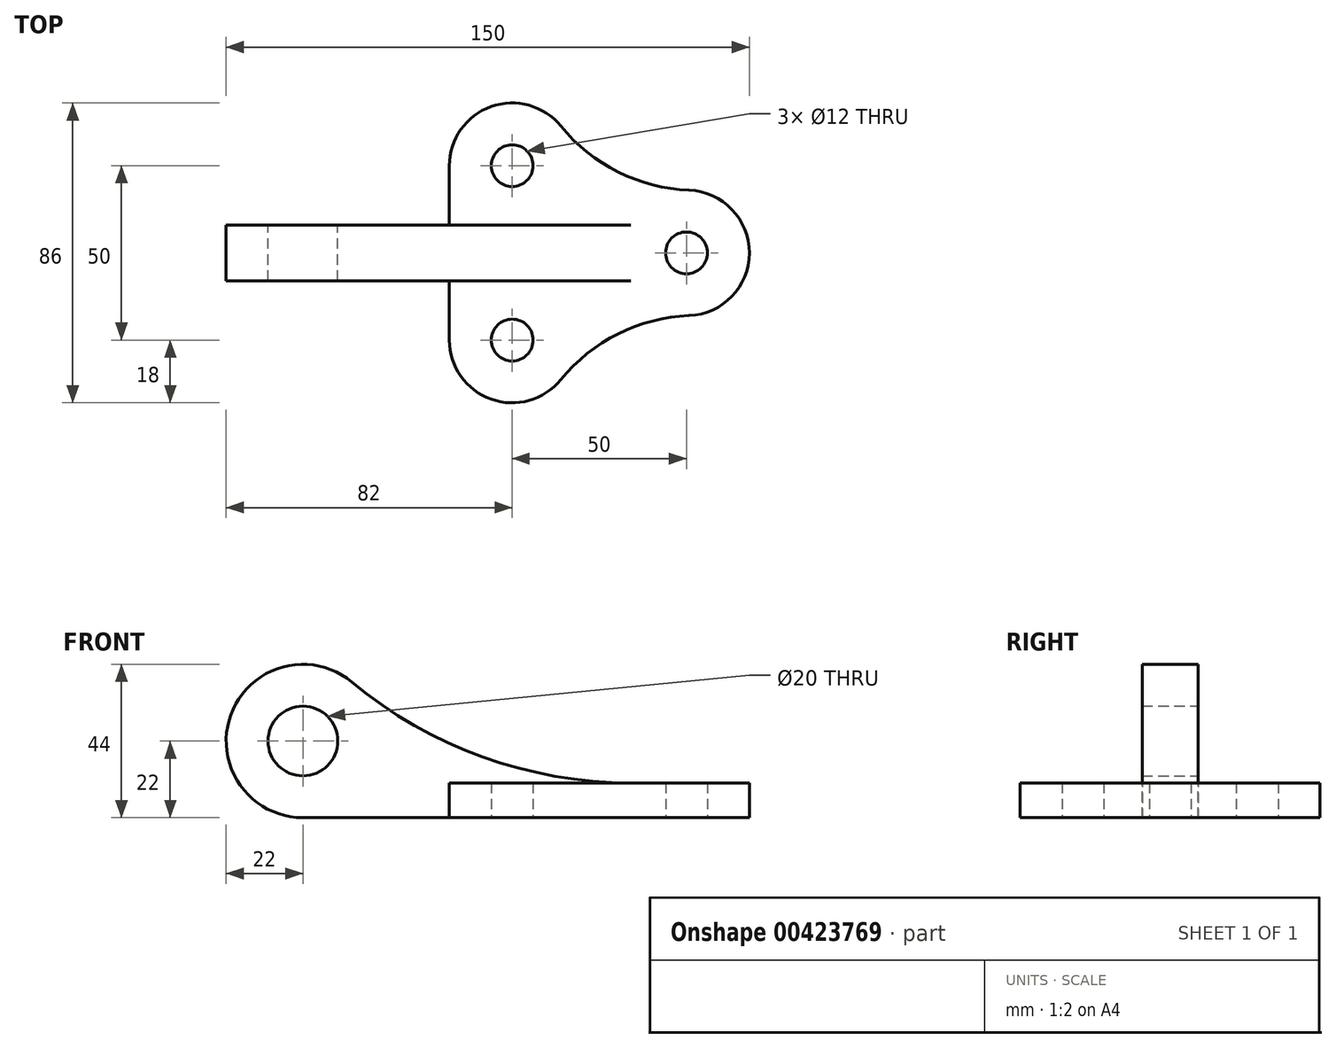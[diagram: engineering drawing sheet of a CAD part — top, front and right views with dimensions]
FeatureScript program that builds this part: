
annotation { "Feature Type Name" : "Feature", "Feature Type Description" : "" }
export const myFeature = defineFeature(function(context is Context, id is Id, definition is map)
    precondition{}
    {
        {
            var Q0;
            Q0=qCreatedBy(makeId("Top.planeOp"),FACE);
            var sketch = newSketch(context, id + "F0", { "sketchPlane" : qUnion([Q0])});
            skCircle(sketch, "E0", {"center": v(0, 25) * mm, "radius": 6 * mm});
            skArc(sketch, "E1", {"start": v(56, 0) * mm, "mid": v(50, 6) * mm, "end": v(44, 0) * mm});
            skArc(sketch, "E2", {"start": v(13.96, 36.37) * mm, "mid": v(-6.03, 41.96) * mm, "end": v(-18, 25) * mm});
            skArc(sketch, "E3", {"start": v(68, 0) * mm, "mid": v(62.98, 12.47) * mm, "end": v(50.72, 17.99) * mm});
            skLineSegment(sketch, "E4.0", {"start": v(-18, 0) * mm, "end": v(-18, 25) * mm});
            skArc(sketch, "E5.filletArc", {"start": v(13.96, 36.37) * mm, "mid": v(30.36, 23.22) * mm, "end": v(50.72, 17.99) * mm});
            skArc(sketch, "E6.MirrorCS", {"start": v(68, 0) * mm, "mid": v(62.98, -12.47) * mm, "end": v(50.72, -17.99) * mm});
            skArc(sketch, "E7.MirrorCS", {"start": v(56, 0) * mm, "mid": v(50, -6) * mm, "end": v(44, 0) * mm});
            skArc(sketch, "E8.MirrorCS", {"start": v(13.96, -36.37) * mm, "mid": v(30.36, -23.22) * mm, "end": v(50.72, -17.99) * mm});
            skArc(sketch, "E9.MirrorCS", {"start": v(13.96, -36.37) * mm, "mid": v(-6.03, -41.96) * mm, "end": v(-18, -25) * mm});
            skLineSegment(sketch, "E10.MirrorCS", {"start": v(-18, 0) * mm, "end": v(-18, -25) * mm});
            skCircle(sketch, "E11.MirrorC", {"center": v(0, -25) * mm, "radius": 6 * mm});
            skSolve(sketch);
        }
        {
            var Q0;
            Q0=makeQuery(id+"F0.imprint","IMPRINT",FACE,{"disambiguationData":[TD([[makeQuery(id+"F0.imprint","IMPRINT",EDGE,{"derivedFrom":sQuery(id+"F0.wireOp",EDGE,"E0")}),-1.0]])]});
            extrude(context, id + "F1", {"entities" : qUnion([Q0]), "depth" : 10 * mm});
        }
        {
            var Q0;
            Q0=qCreatedBy(makeId("Front.planeOp"),FACE);
            var sketch = newSketch(context, id + "F2", { "sketchPlane" : qUnion([Q0])});
            skLineSegment(sketch, "E12", {"start": v(0, 0) * mm, "end": v(-60, 0) * mm});
            skCircle(sketch, "E13", {"center": v(-60, 22) * mm, "radius": 10 * mm});
            skArc(sketch, "E14", {"start": v(-45.93, 38.91) * mm, "mid": v(-80.69, 29.48) * mm, "end": v(-60, 0) * mm});
            skPoint(sketch, "E15.newPointB", {"position": v(0, 10) * mm});
            skArc(sketch, "E15.filletArc", {"start": v(-45.93, 38.91) * mm, "mid": v(-8.49, 17.45) * mm, "end": v(34.02, 10) * mm});
            skLineSegment(sketch, "E16", {"start": v(34.02, 10) * mm, "end": v(34.02, 0) * mm});
            skLineSegment(sketch, "E17", {"start": v(34.02, 0) * mm, "end": v(-60, 0) * mm});
            skSolve(sketch);
        }
        {
            var Q0;
            Q0=makeQuery(id+"F2.imprint","IMPRINT",FACE,{"disambiguationData":[TD([[makeQuery(id+"F2.imprint","IMPRINT",EDGE,{"derivedFrom":sQuery(id+"F2.wireOp",EDGE,"E13")}),-1.0]])]});
            extrude(context, id + "F3", {"entities" : qUnion([Q0]), "operationType" : NewBodyOperationType.ADD, "depth" : 8 * mm, "hasSecondDirection" : true, "secondDirectionOppositeDirection" : true, "secondDirectionDepth" : 8 * mm});
        }
    });
